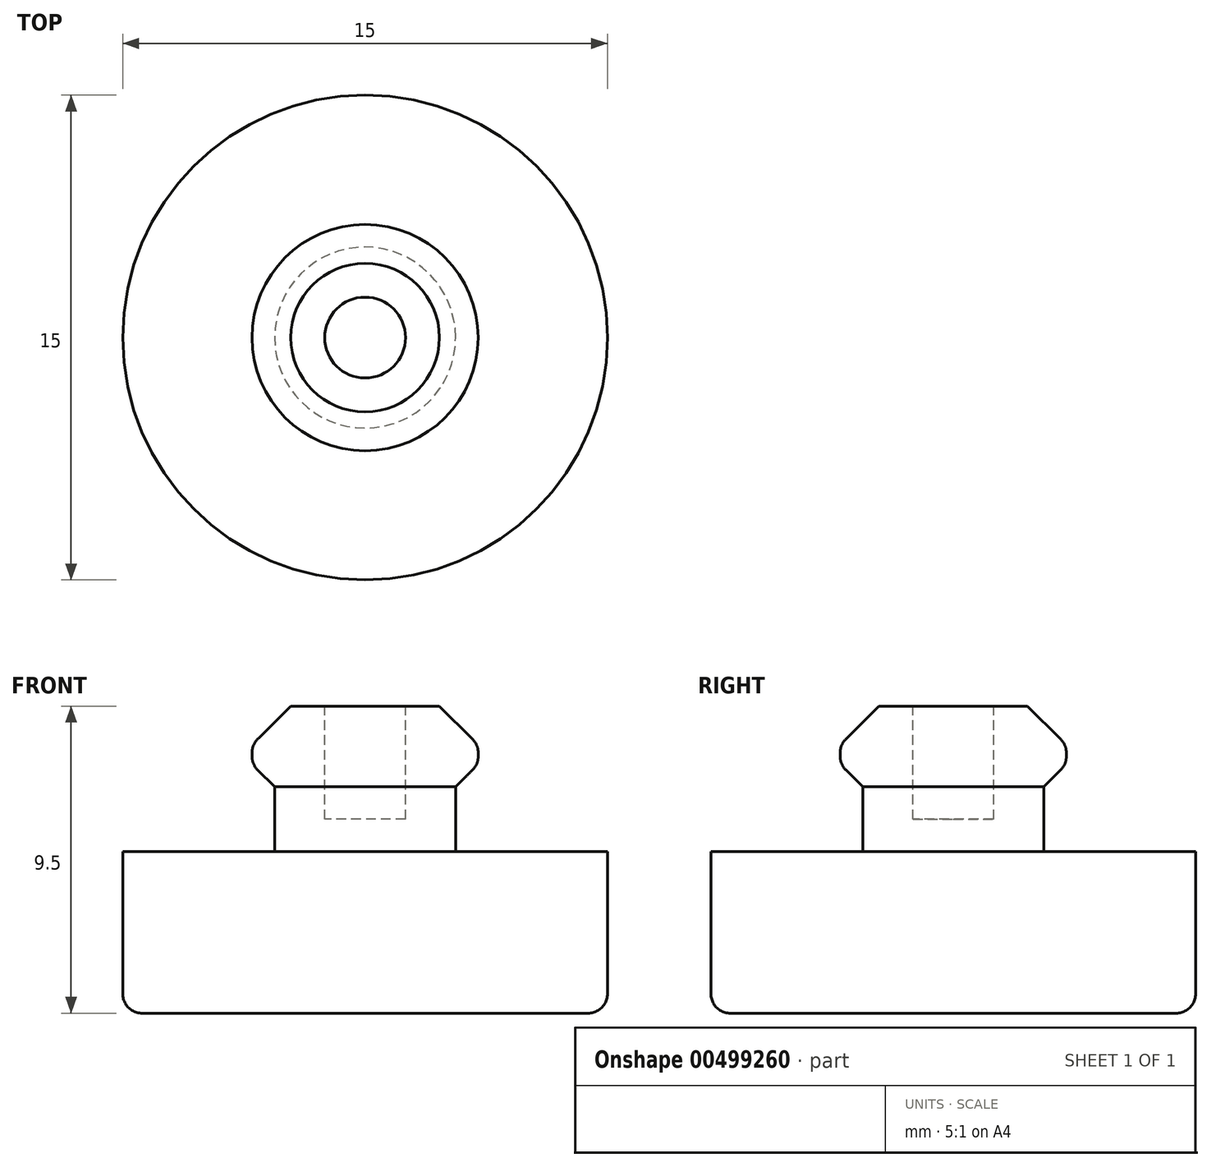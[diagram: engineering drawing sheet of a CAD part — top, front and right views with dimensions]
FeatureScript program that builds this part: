
annotation { "Feature Type Name" : "Feature", "Feature Type Description" : "" }
export const myFeature = defineFeature(function(context is Context, id is Id, definition is map)
    precondition{}
    {
        {
            var Q0;
            Q0=qCreatedBy(makeId("Top.planeOp"),FACE);
            var sketch = newSketch(context, id + "F0", { "sketchPlane" : qUnion([Q0])});
            skCircle(sketch, "E0", {"center": v(0, 0) * mm, "radius": 7.5 * mm});
            skSolve(sketch);
        }
        {
            var Q0;
            Q0 = qSketchRegion(id + "F0", true);
            extrude(context, id + "F1", {"entities" : qUnion([Q0]), "depth" : 5 * mm});
        }
        {
            var Q0;
            Q0=makeQuery(id+"F1.opExtrude","CAP_FACE",FACE,{"disambiguationData":[OSD([sQuery(id+"F0.wireOp",EDGE,"E0")])],"isStart":false});
            var sketch = newSketch(context, id + "F2", { "sketchPlane" : qUnion([Q0])});
            skCircle(sketch, "E1", {"center": v(0, 0) * mm, "radius": 2.8 * mm});
            skSolve(sketch);
        }
        {
            var Q0;
            Q0 = qSketchRegion(id + "F2", true);
            extrude(context, id + "F3", {"entities" : qUnion([Q0]), "operationType" : NewBodyOperationType.ADD, "depth" : 1.5 * mm});
        }
        {
            var Q0;
            Q0=makeQuery(id+"F3.opExtrude","CAP_FACE",FACE,{"disambiguationData":[OSD([sQuery(id+"F2.wireOp",EDGE,"E1")])],"isStart":false});
            var sketch = newSketch(context, id + "F4", { "sketchPlane" : qUnion([Q0])});
            skCircle(sketch, "E2", {"center": v(0, 0) * mm, "radius": 3.5 * mm});
            skSolve(sketch);
        }
        {
            var Q0;
            Q0 = qSketchRegion(id + "F4", true);
            extrude(context, id + "F5", {"entities" : qUnion([Q0]), "operationType" : NewBodyOperationType.ADD, "depth" : 3 * mm});
        }
        {
            var Q0;
            Q0=makeQuery(id+"F5.opExtrude","CAP_EDGE",EDGE,{"disambiguationData":[OSD([sQuery(id+"F4.wireOp",EDGE,"E2")])],"isStart":true});
            var Q1;
            Q1=makeQuery(id+"F5.opExtrude","CAP_EDGE",EDGE,{"disambiguationData":[OSD([sQuery(id+"F4.wireOp",EDGE,"E2")])],"isStart":false});
            chamfer(context, id + "F6", {"entities" : qUnion([Q0, Q1]), "width" : 1.2 * mm, "tangentPropagation" : true});
        }
        {
            var Q0;
            Q0=makeQuery(id+"F5.opExtrude","CAP_FACE",FACE,{"disambiguationData":[OSD([sQuery(id+"F4.wireOp",EDGE,"E2")])],"isStart":false});
            var sketch = newSketch(context, id + "F7", { "sketchPlane" : qUnion([Q0])});
            skCircle(sketch, "E3", {"center": v(0, 0) * mm, "radius": 1.25 * mm});
            skSolve(sketch);
        }
        {
            var Q0;
            Q0 = qSketchRegion(id + "F7", true);
            extrude(context, id + "F8", {"entities" : qUnion([Q0]), "operationType" : NewBodyOperationType.REMOVE, "oppositeDirection" : true, "depth" : 3.5 * mm});
        }
        {
            var Q0;
            Q0=makeQuery(id+"F8.boolean.opBoolean","COPY",EDGE,{"derivedFrom":makeQuery(id+"F8.opExtrude","CAP_EDGE",EDGE,{"disambiguationData":[OSD([sQuery(id+"F7.wireOp",EDGE,"E3")])],"isStart":true})});
            var Q1;
            {var subQ0=sQuery(id+"F4.wireOp",EDGE,"E2");Q1=makeQuery(id+"F6.opChamfer","BLEND_EDGE",EDGE,{"blendedFrom":[makeQuery(id+"F5.opExtrude","CAP_EDGE",EDGE,{"disambiguationData":[OSD([subQ0])],"isStart":true}),makeQuery(id+"F5.opExtrude","SWEPT_FACE",FACE,{"disambiguationData":[OSD([subQ0])]})],"blendedInto":[makeQuery(id+"F5.opExtrude","SWEPT_FACE",FACE,{"disambiguationData":[OSD([subQ0])]})]});}
            var Q2;
            {var subQ0=sQuery(id+"F4.wireOp",EDGE,"E2");Q2=makeQuery(id+"F6.opChamfer","BLEND_EDGE",EDGE,{"blendedFrom":[makeQuery(id+"F5.opExtrude","CAP_EDGE",EDGE,{"disambiguationData":[OSD([subQ0])],"isStart":false}),makeQuery(id+"F5.opExtrude","SWEPT_FACE",FACE,{"disambiguationData":[OSD([subQ0])]})],"blendedInto":[makeQuery(id+"F5.opExtrude","SWEPT_FACE",FACE,{"disambiguationData":[OSD([subQ0])]})]});}
            fillet(context, id + "F9", {"entities" : qUnion([Q0, Q1, Q2]), "radius" : 0.6 * mm, "tangentPropagation" : true, "allowEdgeOverflow" : false});
        }
        {
            var Q0;
            Q0=makeQuery(id+"F1.opExtrude","CAP_EDGE",EDGE,{"disambiguationData":[OSD([sQuery(id+"F0.wireOp",EDGE,"E0")])],"isStart":true});
            fillet(context, id + "F10", {"entities" : qUnion([Q0]), "radius" : 0.6 * mm, "tangentPropagation" : true, "allowEdgeOverflow" : false});
        }
    });
